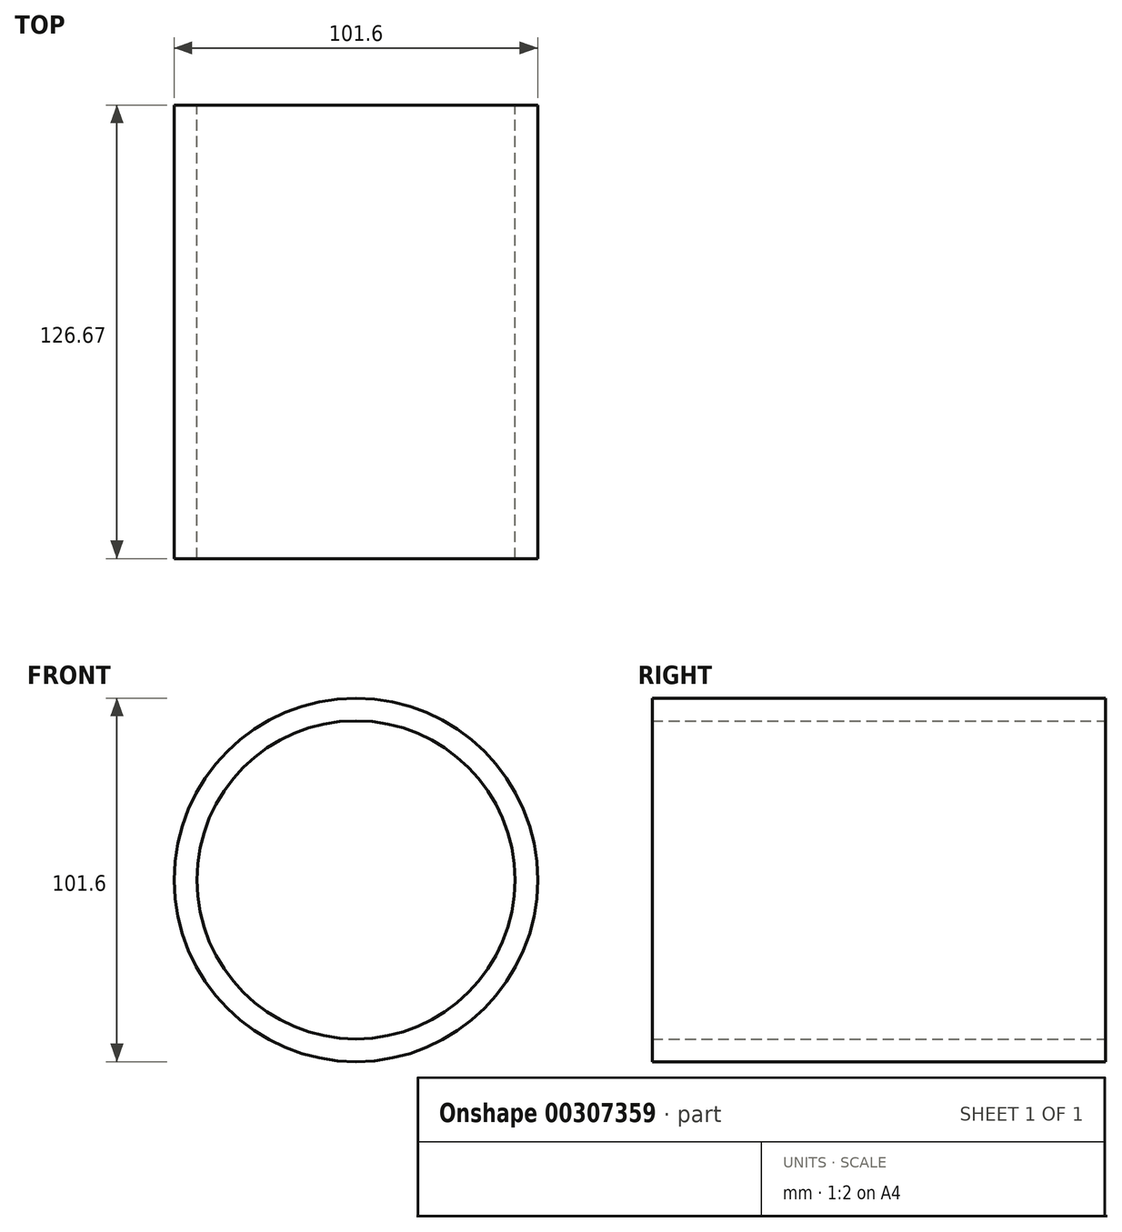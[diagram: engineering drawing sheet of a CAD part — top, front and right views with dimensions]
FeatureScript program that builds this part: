
annotation { "Feature Type Name" : "Feature", "Feature Type Description" : "" }
export const myFeature = defineFeature(function(context is Context, id is Id, definition is map)
    precondition{}
    {
        {
            var Q0;
            Q0=qCreatedBy(makeId("Front.planeOp"),FACE);
            var sketch = newSketch(context, id + "F0", { "sketchPlane" : qUnion([Q0])});
            skCircle(sketch, "E0", {"center": v(0, 0) * mm, "radius": 50.8 * mm});
            skCircle(sketch, "E1", {"center": v(0, 0) * mm, "radius": 44.45 * mm});
            skSolve(sketch);
        }
        {
            var Q0;
            Q0 = qSketchRegion(id + "F0", true);
            extrude(context, id + "F1", {"entities" : qUnion([Q0]), "depth" : 126.67 * mm});
        }
    });
